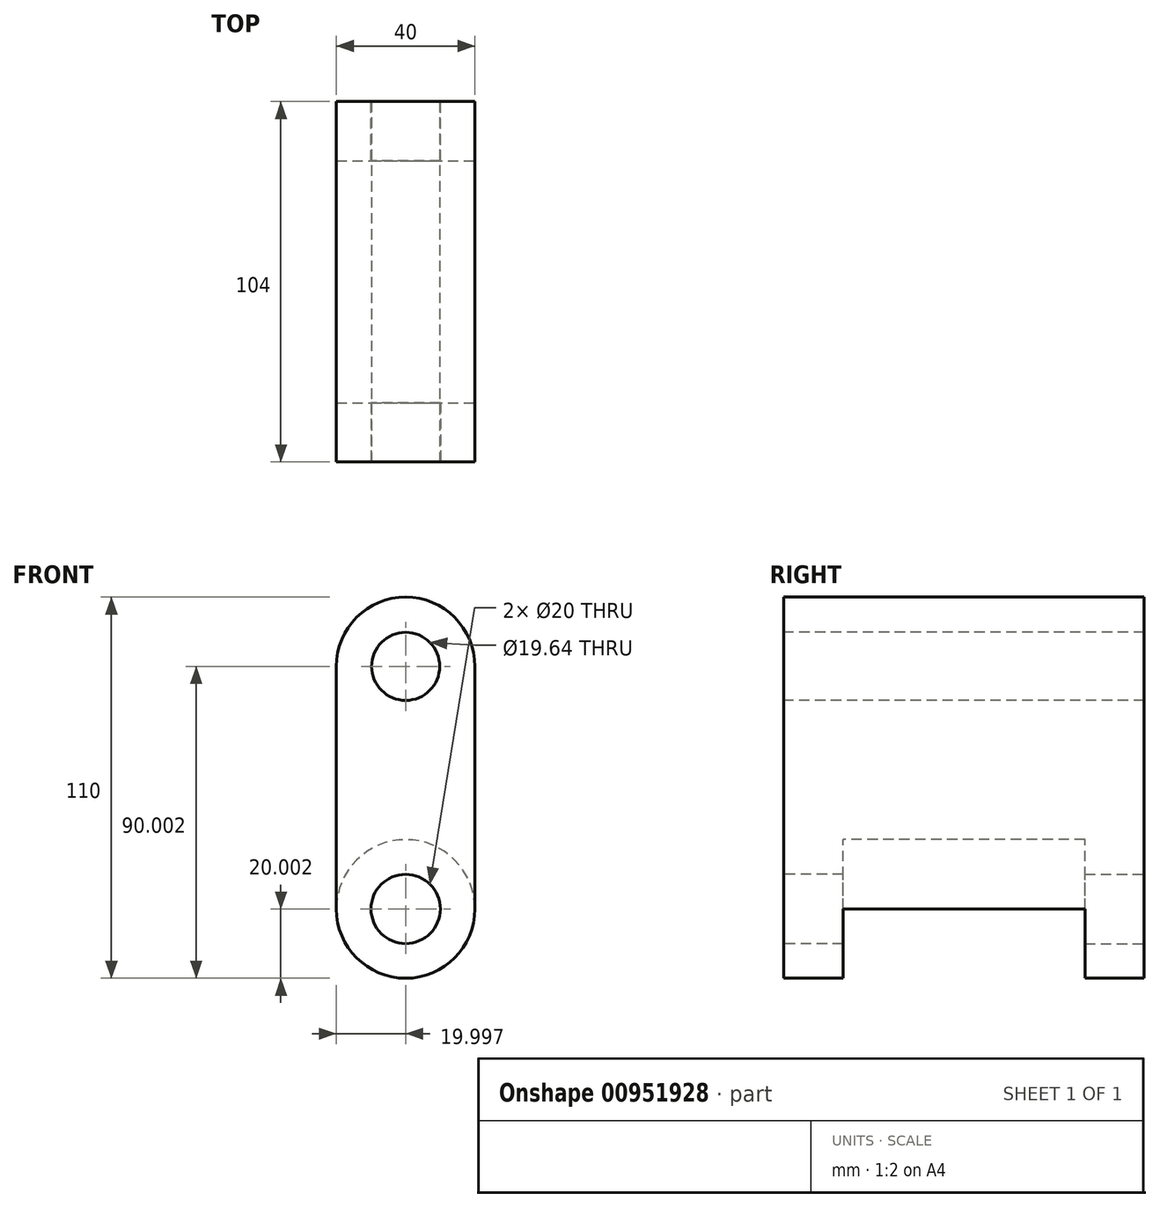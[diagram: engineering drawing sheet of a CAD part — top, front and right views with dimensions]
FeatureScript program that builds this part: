
annotation { "Feature Type Name" : "Feature", "Feature Type Description" : "" }
export const myFeature = defineFeature(function(context is Context, id is Id, definition is map)
    precondition{}
    {
        {
            var Q0;
            Q0=qCreatedBy(makeId("Front.planeOp"),FACE);
            var sketch = newSketch(context, id + "F0", { "sketchPlane" : qUnion([Q0])});
            skLineSegment(sketch, "E0.left", {"start": v(-18.83, -18.25) * mm, "end": v(-18.83, 51.75) * mm});
            skLineSegment(sketch, "E0.right", {"start": v(21.17, -18.25) * mm, "end": v(21.17, 51.75) * mm});
            skArc(sketch, "E1", {"start": v(21.17, 51.75) * mm, "mid": v(1.17, 71.75) * mm, "end": v(-18.83, 51.75) * mm});
            skArc(sketch, "E2", {"start": v(-18.83, -18.25) * mm, "mid": v(1.17, -38.25) * mm, "end": v(21.17, -18.25) * mm});
            skSolve(sketch);
        }
        {
            var Q0;
            Q0=makeQuery(id+"F0.imprint","IMPRINT",FACE,{"disambiguationData":[TD([[makeQuery(id+"F0.imprint","IMPRINT",EDGE,{"derivedFrom":sQuery(id+"F0.wireOp",EDGE,"E0.left")}),-1.0]])]});
            extrude(context, id + "F1", {"entities" : qUnion([Q0]), "depth" : 17.1 * mm, "offsetDistance" : 25 * mm});
        }
        {
            var Q0;
            Q0=makeQuery(id+"F1.opExtrude","CAP_FACE",FACE,{"disambiguationData":[OSD([sQuery(id+"F0.wireOp",EDGE,"E0.left"),sQuery(id+"F0.wireOp",EDGE,"E0.right"),sQuery(id+"F0.wireOp",EDGE,"E1"),sQuery(id+"F0.wireOp",EDGE,"E2")])],"isStart":false});
            var sketch = newSketch(context, id + "F2", { "sketchPlane" : qUnion([Q0])});
            skCircle(sketch, "E3", {"center": v(1.17, 51.75) * mm, "radius": 9.82 * mm});
            skSolve(sketch);
        }
        {
            var Q0;
            Q0 = qSketchRegion(id + "F2", true);
            extrude(context, id + "F3", {"entities" : qUnion([Q0]), "operationType" : NewBodyOperationType.REMOVE, "oppositeDirection" : true, "depth" : 25 * mm, "offsetDistance" : 25 * mm});
        }
        {
            var Q0;
            Q0=makeQuery(id+"F1.opExtrude","CAP_FACE",FACE,{"disambiguationData":[OSD([sQuery(id+"F0.wireOp",EDGE,"E0.left"),sQuery(id+"F0.wireOp",EDGE,"E0.right"),sQuery(id+"F0.wireOp",EDGE,"E1"),sQuery(id+"F0.wireOp",EDGE,"E2")])],"isStart":true});
            var sketch = newSketch(context, id + "F4", { "sketchPlane" : qUnion([Q0])});
            skCircle(sketch, "E4", {"center": v(-1.17, -18.25) * mm, "radius": 20 * mm});
            skSolve(sketch);
        }
        {
            var Q0;
            {var subQ0=sQuery(id+"F4.wireOp",EDGE,"E4");Q0=makeQuery(id+"F4.imprint","IMPRINT",FACE,{"disambiguationData":[TD([[makeQuery(id+"F4.imprint","IMPRINT",EDGE,{"disambiguationData":[OD(0.0)],"derivedFrom":subQ0}),-1.0]])]});}
            extrude(context, id + "F5", {"entities" : qUnion([Q0]), "operationType" : NewBodyOperationType.ADD, "depth" : 34.9 * mm, "offsetDistance" : 25 * mm});
        }
        {
            var Q0;
            Q0=makeQuery(id+"F1.opExtrude","CAP_FACE",FACE,{"disambiguationData":[OSD([sQuery(id+"F0.wireOp",EDGE,"E0.left"),sQuery(id+"F0.wireOp",EDGE,"E0.right"),sQuery(id+"F0.wireOp",EDGE,"E1"),sQuery(id+"F0.wireOp",EDGE,"E2")])],"isStart":false});
            var sketch = newSketch(context, id + "F6", { "sketchPlane" : qUnion([Q0])});
            skCircle(sketch, "E5", {"center": v(1.17, -18.25) * mm, "radius": 10 * mm});
            skSolve(sketch);
        }
        {
            var Q0;
            Q0=makeQuery(id+"F6.imprint","IMPRINT",FACE,{"disambiguationData":[TD([[makeQuery(id+"F6.imprint","IMPRINT",EDGE,{"derivedFrom":sQuery(id+"F6.wireOp",EDGE,"E5")}),1.0]])]});
            extrude(context, id + "F7", {"entities" : qUnion([Q0]), "operationType" : NewBodyOperationType.REMOVE, "endBound" : BoundingType.THROUGH_ALL, "oppositeDirection" : true, "depth" : 25 * mm, "offsetDistance" : 25 * mm});
        }
        {
            var Q0;
            Q0=makeQuery(id+"F1.opExtrude","SWEPT_BODY",BODY,{"disambiguationData":[OSD([sQuery(id+"F0.wireOp",EDGE,"E0.left"),sQuery(id+"F0.wireOp",EDGE,"E0.right"),sQuery(id+"F0.wireOp",EDGE,"E1"),sQuery(id+"F0.wireOp",EDGE,"E2")])]});
            var Q1;
            Q1=makeQuery(id+"F5.opExtrude","CAP_FACE",FACE,{"disambiguationData":[OSD([sQuery(id+"F4.wireOp",EDGE,"E4")])],"isStart":false});
            mirror(context, id + "F8", {"operationType" : NewBodyOperationType.ADD, "entities" : qUnion([Q0]), "mirrorPlane" : qUnion([Q1])});
        }
    });
